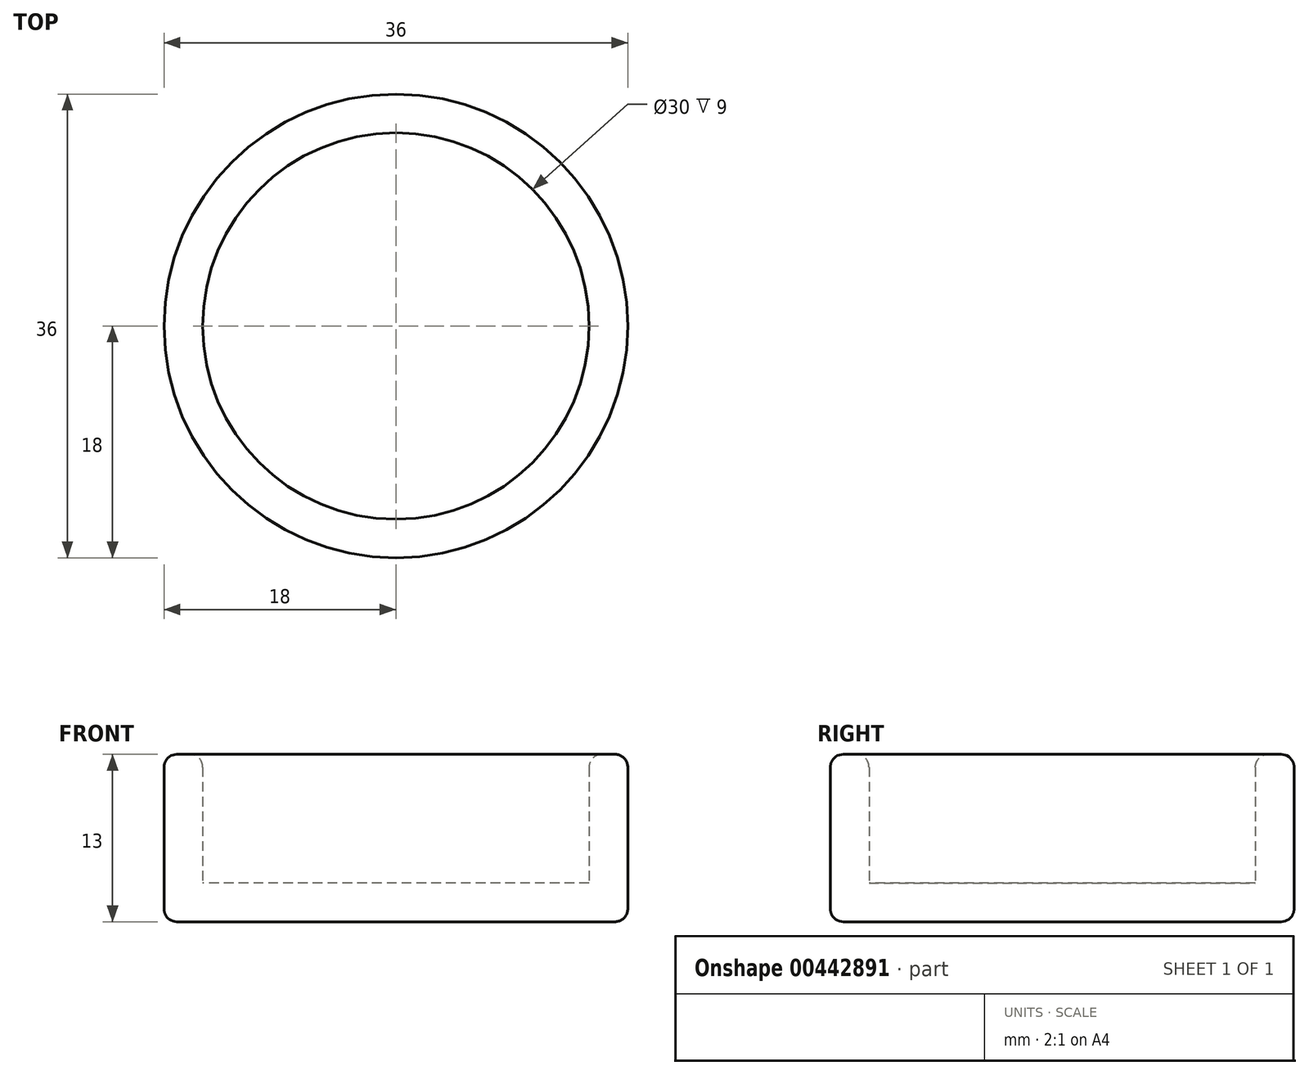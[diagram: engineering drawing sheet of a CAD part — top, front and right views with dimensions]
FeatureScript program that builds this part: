
annotation { "Feature Type Name" : "Feature", "Feature Type Description" : "" }
export const myFeature = defineFeature(function(context is Context, id is Id, definition is map)
    precondition{}
    {
        {
            var Q0;
            Q0=qCreatedBy(makeId("Top.planeOp"),FACE);
            var sketch = newSketch(context, id + "F0", { "sketchPlane" : qUnion([Q0])});
            skCircle(sketch, "E0", {"center": v(0, 0) * mm, "radius": 18 * mm});
            skCircle(sketch, "E1", {"center": v(0, 0) * mm, "radius": 15 * mm});
            skSolve(sketch);
        }
        {
            var Q0;
            Q0=makeQuery(id+"F0.imprint","IMPRINT",FACE,{"disambiguationData":[TD([[makeQuery(id+"F0.imprint","IMPRINT",EDGE,{"derivedFrom":sQuery(id+"F0.wireOp",EDGE,"E0")}),1.0]])]});
            extrude(context, id + "F1", {"entities" : qUnion([Q0]), "depth" : 10 * mm});
        }
        {
            var Q0;
            Q0=makeQuery(id+"F0.imprint","IMPRINT",FACE,{"disambiguationData":[TD([[makeQuery(id+"F0.imprint","IMPRINT",EDGE,{"derivedFrom":sQuery(id+"F0.wireOp",EDGE,"E0")}),1.0]])]});
            var sketch = newSketch(context, id + "F2", { "sketchPlane" : qUnion([Q0])});
            skCircle(sketch, "E2", {"center": v(0, 0) * mm, "radius": 18 * mm});
            skSolve(sketch);
        }
        {
            var Q0;
            Q0 = qSketchRegion(id + "F2", true);
            extrude(context, id + "F3", {"entities" : qUnion([Q0]), "operationType" : NewBodyOperationType.ADD, "depth" : -3 * mm});
        }
        {
            var Q0;
            Q0=makeQuery(id+"F1.opExtrude","CAP_EDGE",EDGE,{"disambiguationData":[OSD([sQuery(id+"F0.wireOp",EDGE,"E0")])],"isStart":false});
            var Q1;
            Q1=makeQuery(id+"F1.opExtrude","CAP_EDGE",EDGE,{"disambiguationData":[OSD([sQuery(id+"F0.wireOp",EDGE,"E1")])],"isStart":false});
            var Q2;
            Q2=makeQuery(id+"F3.opExtrude","CAP_EDGE",EDGE,{"disambiguationData":[OSD([sQuery(id+"F2.wireOp",EDGE,"E2")])],"isStart":false});
            fillet(context, id + "F4", {"entities" : qUnion([Q0, Q1, Q2]), "radius" : 1 * mm, "tangentPropagation" : true, "allowEdgeOverflow" : false});
        }
    });
